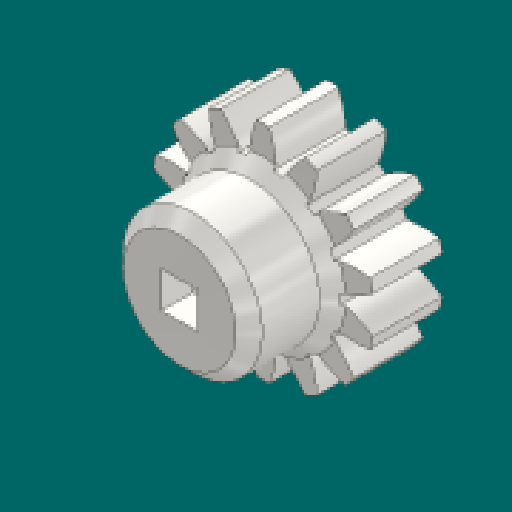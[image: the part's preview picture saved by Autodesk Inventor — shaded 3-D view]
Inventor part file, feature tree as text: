
AUTODESK INVENTOR PART (.ipt)
format: ipt  version: 2023.1 (Build 271208000, 208)  size: 316,416 bytes
history: native  units: mm (DEFAULTED — no unit token found)
features: sketch x5, extrude x4, plane x4, other x3, chamfer x3, projected_geometry x1
ambient origin geometry x8: Origin, YZ Plane, XZ Plane, XY Plane, X Axis, Y Axis, Z Axis, Center Point
bodies: Solid1 (feature_tree)
feature tree (20):
  extrude  "Extrusion1"  Depth=6.35mm TaperAngle=0.0deg
  plane  "Work Plane1"
  plane  "Work Plane2"
  plane  "Work Plane3"
  other  "Spur Gear"
  extrude  "Extrusion2"  Depth=76.2mm TaperAngle=0.0deg
  sketch  "Sketch4"  dims[d16=0.0mm d17=0.0mm d18=0.0mm d19=17.78mm]
  plane  "Work Plane4"
  extrude  "Extrusion3"  TaperAngle=0.0deg  [1 undecoded]
  chamfer  "Chamfer1"  Distance=17.78mm
  chamfer  "Chamfer2"  Distance=17.78mm
  extrude  "Extrusion4"  Depth=3.302mm
  chamfer  "Chamfer3"  [1 undecoded]
  sketch  "Sketch1"  dims[d0=20.32mm d1=6.35mm d2=0.0mm]
  sketch  "Sketch2"  dims[d3=17.78mm d4=76.2mm d5=0.0mm]
  other  "Srf1"
  sketch  "Sketch3"  dims[d6=0.0mm d7=2.243995mm d9=0.0mm d14=0.0mm d15=17.78mm]
  projected_geometry  "Projected Loop1"
  sketch  "Sketch5"  dims[d20=3.302mm d21=3.302mm d22=0.0mm d23=0.0mm d24=12.7mm d25=7.62mm d26=0.0mm d27=1.2mm d28=3.175mm d29=45.0deg d30=1.2mm d31=3.175mm d32=45.0deg d33=6.604mm d34=6.604mm d35=11.1125mm d36=0.0mm d37=1.651mm d38=3.175mm d39=45.0deg]
  other  "Pitch Diameter"
note: 2 required parameter values undecoded (feature->parameter linkage not recoverable at this tier; creation-order binding heuristic only, values carry confidence <= 0.55)
